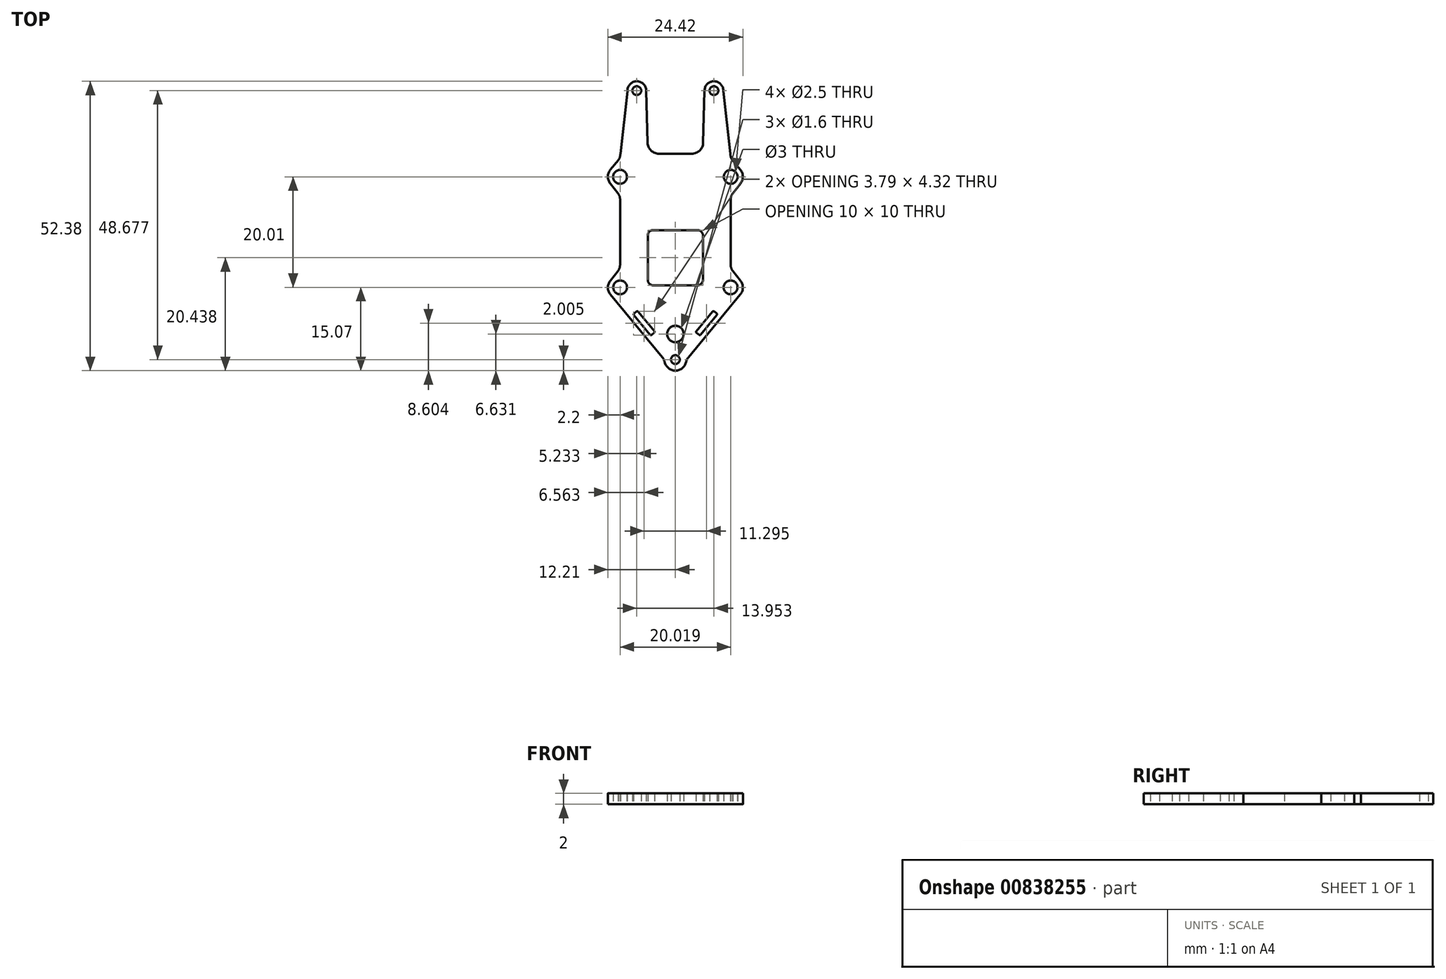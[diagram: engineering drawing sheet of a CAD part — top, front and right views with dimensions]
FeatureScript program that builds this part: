
annotation { "Feature Type Name" : "Feature", "Feature Type Description" : "" }
export const myFeature = defineFeature(function(context is Context, id is Id, definition is map)
    precondition{}
    {
        {
            var Q0;
            Q0=qCreatedBy(makeId("Top.planeOp"),FACE);
            var sketch = newSketch(context, id + "F0", { "sketchPlane" : qUnion([Q0])});
            skCircle(sketch, "E0", {"center": v(10, 10) * mm, "radius": 1.25 * mm});
            skCircle(sketch, "E1.MirrorC", {"center": v(10, -10) * mm, "radius": 1.25 * mm});
            skLineSegment(sketch, "E2.top", {"start": v(13.5, 13.5) * mm, "end": v(10, 13.5) * mm, "construction": true});
            skLineSegment(sketch, "E2.left", {"start": v(13.5, -13.5) * mm, "end": v(13.5, 13.5) * mm, "construction": true});
            skLineSegment(sketch, "E3", {"start": v(10, 5.88) * mm, "end": v(10, -5.88) * mm});
            skPoint(sketch, "E4.visualSharp", {"position": v(12.48, 10) * mm});
            skPoint(sketch, "E5.visualSharp", {"position": v(10, 6.5) * mm});
            skArc(sketch, "E5.filletArc", {"start": v(10.38, 7.03) * mm, "mid": v(10.1, 6.48) * mm, "end": v(10, 5.88) * mm});
            skArc(sketch, "E6.filletArc", {"start": v(9.95, 14.2) * mm, "mid": v(10.04, 13.58) * mm, "end": v(10.32, 13.03) * mm});
            skLineSegment(sketch, "E7", {"start": v(10.32, 13.03) * mm, "end": v(11.75, 11.3) * mm});
            skLineSegment(sketch, "E8", {"start": v(11.77, 8.78) * mm, "end": v(10.38, 7.03) * mm});
            skPoint(sketch, "E9.visualSharp", {"position": v(12.79, 10.05) * mm});
            skArc(sketch, "E9.filletArc", {"start": v(11.77, 8.78) * mm, "mid": v(12.2, 10.05) * mm, "end": v(11.75, 11.3) * mm});
            skLineSegment(sketch, "E10.MirrorCS", {"start": v(11.77, -8.78) * mm, "end": v(10.38, -7.03) * mm});
            skPoint(sketch, "E11.MirrorP", {"position": v(12.48, -10) * mm});
            skLineSegment(sketch, "E12.MirrorCS", {"start": v(10.32, -13.03) * mm, "end": v(11.75, -11.3) * mm});
            skArc(sketch, "E13.MirrorCS", {"start": v(11.77, -8.78) * mm, "mid": v(12.2, -10.05) * mm, "end": v(11.75, -11.3) * mm});
            skArc(sketch, "E14.MirrorCS", {"start": v(10.38, -7.03) * mm, "mid": v(10.1, -6.48) * mm, "end": v(10, -5.88) * mm});
            skLineSegment(sketch, "E15.MirrorCS", {"start": v(-10.32, 13.03) * mm, "end": v(-11.75, 11.3) * mm});
            skLineSegment(sketch, "E16.MirrorCS", {"start": v(-13.5, 13.5) * mm, "end": v(-10, 13.5) * mm, "construction": true});
            skArc(sketch, "E17.MirrorCS", {"start": v(-11.77, 8.78) * mm, "mid": v(-12.2, 10.05) * mm, "end": v(-11.75, 11.3) * mm});
            skArc(sketch, "E18.MirrorCS", {"start": v(-9.95, 14.2) * mm, "mid": v(-10.04, 13.58) * mm, "end": v(-10.32, 13.03) * mm});
            skLineSegment(sketch, "E19.MirrorCS", {"start": v(-11.77, -8.78) * mm, "end": v(-10.38, -7.03) * mm});
            skArc(sketch, "E20.MirrorCS", {"start": v(-10.38, -7.03) * mm, "mid": v(-10.1, -6.48) * mm, "end": v(-10, -5.88) * mm});
            skLineSegment(sketch, "E21.MirrorCS", {"start": v(-11.77, 8.78) * mm, "end": v(-10.38, 7.03) * mm});
            skArc(sketch, "E22.MirrorCS", {"start": v(-10.38, 7.03) * mm, "mid": v(-10.1, 6.48) * mm, "end": v(-10, 5.88) * mm});
            skCircle(sketch, "E23.MirrorC", {"center": v(-10, -10) * mm, "radius": 1.25 * mm});
            skLineSegment(sketch, "E24.MirrorCS", {"start": v(-10.32, -13.03) * mm, "end": v(-11.75, -11.3) * mm});
            skCircle(sketch, "E25.MirrorC", {"center": v(-10, 10) * mm, "radius": 1.25 * mm});
            skArc(sketch, "E26.MirrorCS", {"start": v(-11.77, -8.78) * mm, "mid": v(-12.2, -10.05) * mm, "end": v(-11.75, -11.3) * mm});
            skPoint(sketch, "E27.MirrorP", {"position": v(-12.48, 10) * mm});
            skLineSegment(sketch, "E28.MirrorCS", {"start": v(-10, 5.88) * mm, "end": v(-10, -5.88) * mm});
            skPoint(sketch, "E29.MirrorP", {"position": v(-10, 6.5) * mm});
            skPoint(sketch, "E30.MirrorP", {"position": v(-12.48, -10) * mm});
            skPoint(sketch, "E31.MirrorP", {"position": v(-12.79, 10.05) * mm});
            skLineSegment(sketch, "E32.MirrorCS", {"start": v(-13.5, -13.5) * mm, "end": v(-13.5, 13.5) * mm, "construction": true});
            skPoint(sketch, "E33.MirrorP", {"position": v(-9.95, 13.5) * mm});
            skPoint(sketch, "E34.MirrorCS.end.orphan", {"position": v(-10.32, -13.03) * mm});
            skPoint(sketch, "E34.MirrorCS.start.orphan", {"position": v(-7.95, -16.6) * mm});
            skPoint(sketch, "E35.MirrorCS.end.orphan", {"position": v(10.32, -13.03) * mm});
            skPoint(sketch, "E35.MirrorCS.start.orphan", {"position": v(9.95, -14.2) * mm});
            skLineSegment(sketch, "E36", {"start": v(-10.32, -13.03) * mm, "end": v(-2.37, -22.64) * mm});
            skLineSegment(sketch, "E37.MirrorCS", {"start": v(10.32, -13.03) * mm, "end": v(2.37, -22.64) * mm});
            skPoint(sketch, "E38.visualSharp", {"position": v(0, -25.5) * mm});
            skCircle(sketch, "E39", {"center": v(0, -23.07) * mm, "radius": 0.8 * mm});
            skArc(sketch, "E40.0", {"start": v(-1.95, -23.49) * mm, "mid": v(0, -25.07) * mm, "end": v(1.95, -23.49) * mm});
            skPoint(sketch, "E41.visualSharp", {"position": v(-2, -23.08) * mm});
            skArc(sketch, "E41.filletArc", {"start": v(-1.95, -23.49) * mm, "mid": v(-2.11, -23.04) * mm, "end": v(-2.37, -22.64) * mm});
            skPoint(sketch, "E42.visualSharp", {"position": v(2, -23.08) * mm});
            skArc(sketch, "E42.filletArc", {"start": v(2.37, -22.64) * mm, "mid": v(2.11, -23.04) * mm, "end": v(1.95, -23.49) * mm});
            skPoint(sketch, "E43.MirrorP", {"position": v(9.95, 13.5) * mm});
            skLineSegment(sketch, "E44", {"start": v(-2.97, 14.2) * mm, "end": v(2.97, 14.2) * mm});
            skArc(sketch, "E45.filletArc", {"start": v(2.97, 14.2) * mm, "mid": v(4.4, 14.77) * mm, "end": v(5.02, 16.19) * mm});
            skLineSegment(sketch, "E46.MirrorCS", {"start": v(-6.98, 25.61) * mm, "end": v(-6.98, 23.4) * mm, "construction": true});
            skCircle(sketch, "E47.MirrorC", {"center": v(-6.98, 25.61) * mm, "radius": 0.8 * mm});
            skPoint(sketch, "E48.MirrorP", {"position": v(-9.05, 28.16) * mm});
            skLineSegment(sketch, "E49.MirrorCS", {"start": v(-5.28, 25.57) * mm, "end": v(-5.02, 16.19) * mm});
            skArc(sketch, "E50.MirrorCS", {"start": v(-2.97, 14.2) * mm, "mid": v(-4.4, 14.77) * mm, "end": v(-5.02, 16.19) * mm});
            skLineSegment(sketch, "E51", {"start": v(-9.95, 14.2) * mm, "end": v(-8.68, 25.56) * mm});
            skArc(sketch, "E52.0", {"start": v(-5.28, 25.6) * mm, "mid": v(-6.95, 27.31) * mm, "end": v(-8.68, 25.65) * mm});
            skPoint(sketch, "E53.visualSharp", {"position": v(-8.68, 25.61) * mm});
            skArc(sketch, "E53.filletArc", {"start": v(-8.68, 25.56) * mm, "mid": v(-8.68, 25.6) * mm, "end": v(-8.68, 25.65) * mm});
            skPoint(sketch, "E54.visualSharp", {"position": v(-5.28, 25.6) * mm});
            skArc(sketch, "E54.filletArc", {"start": v(-5.28, 25.6) * mm, "mid": v(-5.28, 25.59) * mm, "end": v(-5.28, 25.57) * mm});
            skArc(sketch, "E55.MirrorCS", {"start": v(8.68, 25.56) * mm, "mid": v(8.68, 25.6) * mm, "end": v(8.68, 25.65) * mm});
            skArc(sketch, "E56.MirrorCS", {"start": v(5.28, 25.6) * mm, "mid": v(5.28, 25.59) * mm, "end": v(5.28, 25.57) * mm});
            skCircle(sketch, "E57.MirrorC", {"center": v(6.98, 25.61) * mm, "radius": 0.8 * mm});
            skPoint(sketch, "E58.MirrorP", {"position": v(8.68, 25.61) * mm});
            skPoint(sketch, "E59.MirrorP", {"position": v(9.05, 28.16) * mm});
            skPoint(sketch, "E60.MirrorP", {"position": v(5.28, 25.6) * mm});
            skLineSegment(sketch, "E61.MirrorCS", {"start": v(5.28, 25.57) * mm, "end": v(5.02, 16.19) * mm});
            skArc(sketch, "E62.MirrorCS", {"start": v(5.28, 25.6) * mm, "mid": v(6.95, 27.31) * mm, "end": v(8.68, 25.65) * mm});
            skLineSegment(sketch, "E63.MirrorCS", {"start": v(6.98, 25.61) * mm, "end": v(6.98, 23.4) * mm, "construction": true});
            skLineSegment(sketch, "E64.MirrorCS", {"start": v(9.95, 14.2) * mm, "end": v(8.68, 25.56) * mm});
            skPoint(sketch, "E65.MirrorCS.start.orphan", {"position": v(9.95, 14.2) * mm});
            skLineSegment(sketch, "E66.0", {"start": v(-7.5, -15.01) * mm, "end": v(-4.57, -18.56) * mm});
            skLineSegment(sketch, "E67.0", {"start": v(-6.73, -14.38) * mm, "end": v(-3.8, -17.92) * mm});
            skLineSegment(sketch, "E68", {"start": v(-7.01, -14.35) * mm, "end": v(-7.47, -14.73) * mm});
            skLineSegment(sketch, "E69", {"start": v(-3.82, -18.2) * mm, "end": v(-4.28, -18.58) * mm});
            skPoint(sketch, "E70.visualSharp", {"position": v(-6.86, -14.22) * mm});
            skArc(sketch, "E70.filletArc", {"start": v(-6.73, -14.38) * mm, "mid": v(-6.86, -14.3) * mm, "end": v(-7.01, -14.35) * mm});
            skArc(sketch, "E71.filletArc", {"start": v(-7.47, -14.73) * mm, "mid": v(-7.54, -14.87) * mm, "end": v(-7.5, -15.01) * mm});
            skArc(sketch, "E72.filletArc", {"start": v(-4.57, -18.56) * mm, "mid": v(-4.43, -18.63) * mm, "end": v(-4.28, -18.58) * mm});
            skPoint(sketch, "E73.visualSharp", {"position": v(-3.67, -18.07) * mm});
            skArc(sketch, "E73.filletArc", {"start": v(-3.82, -18.2) * mm, "mid": v(-3.75, -18.07) * mm, "end": v(-3.8, -17.92) * mm});
            skCircle(sketch, "E74", {"center": v(0, -18.44) * mm, "radius": 1.5 * mm});
            skLineSegment(sketch, "E75.bottom", {"start": v(18.76, -26.87) * mm, "end": v(-18.76, -26.87) * mm, "construction": true});
            skLineSegment(sketch, "E75.top", {"start": v(18.76, 26.87) * mm, "end": v(-18.76, 26.87) * mm, "construction": true});
            skLineSegment(sketch, "E75.left", {"start": v(18.76, -26.87) * mm, "end": v(18.76, 26.87) * mm, "construction": true});
            skLineSegment(sketch, "E75.right", {"start": v(-18.76, -26.87) * mm, "end": v(-18.76, 26.87) * mm, "construction": true});
            skLineSegment(sketch, "E76.bottom", {"start": v(4, -9.63) * mm, "end": v(-4, -9.63) * mm});
            skLineSegment(sketch, "E76.top", {"start": v(4, 0.37) * mm, "end": v(-4, 0.37) * mm});
            skLineSegment(sketch, "E76.left", {"start": v(5, -8.63) * mm, "end": v(5, -0.63) * mm});
            skLineSegment(sketch, "E76.right", {"start": v(-5, -8.63) * mm, "end": v(-5, -0.63) * mm});
            skPoint(sketch, "E76.middle", {"position": v(0, -4.63) * mm});
            skPoint(sketch, "E77.visualSharp", {"position": v(-5, 0.37) * mm});
            skArc(sketch, "E77.filletArc", {"start": v(-4, 0.37) * mm, "mid": v(-4.7, 0.07) * mm, "end": v(-5, -0.63) * mm});
            skPoint(sketch, "E78.visualSharp", {"position": v(5, 0.37) * mm});
            skArc(sketch, "E78.filletArc", {"start": v(5, -0.63) * mm, "mid": v(4.7, 0.07) * mm, "end": v(4, 0.37) * mm});
            skPoint(sketch, "E79.visualSharp", {"position": v(5, -9.63) * mm});
            skArc(sketch, "E79.filletArc", {"start": v(4, -9.63) * mm, "mid": v(4.7, -9.34) * mm, "end": v(5, -8.63) * mm});
            skPoint(sketch, "E80.visualSharp", {"position": v(-5, -9.63) * mm});
            skArc(sketch, "E80.filletArc", {"start": v(-5, -8.63) * mm, "mid": v(-4.7, -9.34) * mm, "end": v(-4, -9.63) * mm});
            skArc(sketch, "E81.MirrorCS", {"start": v(6.73, -14.38) * mm, "mid": v(6.86, -14.3) * mm, "end": v(7.01, -14.35) * mm});
            skArc(sketch, "E82.MirrorCS", {"start": v(3.82, -18.2) * mm, "mid": v(3.75, -18.07) * mm, "end": v(3.8, -17.92) * mm});
            skArc(sketch, "E83.MirrorCS", {"start": v(4.57, -18.56) * mm, "mid": v(4.43, -18.63) * mm, "end": v(4.28, -18.58) * mm});
            skLineSegment(sketch, "E84.MirrorCS", {"start": v(7.01, -14.35) * mm, "end": v(7.47, -14.73) * mm});
            skLineSegment(sketch, "E85.MirrorCS", {"start": v(3.82, -18.2) * mm, "end": v(4.28, -18.58) * mm});
            skArc(sketch, "E86.MirrorCS", {"start": v(7.47, -14.73) * mm, "mid": v(7.54, -14.87) * mm, "end": v(7.5, -15.01) * mm});
            skPoint(sketch, "E87.MirrorP", {"position": v(6.86, -14.22) * mm});
            skPoint(sketch, "E88.MirrorP", {"position": v(3.67, -18.07) * mm});
            skLineSegment(sketch, "E89.MirrorCS", {"start": v(7.5, -15.01) * mm, "end": v(4.57, -18.56) * mm});
            skLineSegment(sketch, "E90.MirrorCS", {"start": v(6.73, -14.38) * mm, "end": v(3.8, -17.92) * mm});
            skSolve(sketch);
        }
        {
            var Q0;
            Q0 = qSketchRegion(id + "F0", true);
            extrude(context, id + "F1", {"entities" : qUnion([Q0]), "depth" : 2 * mm, "offsetDistance" : 25 * mm});
        }
    });
